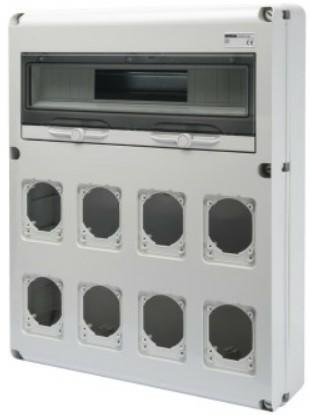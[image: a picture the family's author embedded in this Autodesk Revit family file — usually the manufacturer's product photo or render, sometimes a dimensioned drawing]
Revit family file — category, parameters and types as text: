
# Revit family: Building-QuadriIEC309-GEWISS-68QDIN-QUADRI-PRESE-20MOD_8PRESE
name_source: partatom
category: Apparecchi elettrici
units: mm (PartAtom-declared; Revit-internal decimal feet)

## family parameters
Condiviso = No
Host = Superficie
Mantenere orientamento annotazione = Sì
Punto di calcolo locali = Sì
Quota connettore circolare = Usa diametro
Taglio con vuoti quando caricato = No
Tipo di parte = Normale

## types (1)
- GW68013N - Q-DIN 20M 8FLANGE PR.16/32A IP65
    Catalogo = BUILDING
    Catalogo Serie = 68 QDIN
    Classe isolamento = II
    Codice EAN = 8011564744905
    Codice Electrocod = 2242
    Colore = Grigio RAL 7035
    Conformità normativa = EN 60208 - EN 60670-1 - IEC 60670-24
    Descrizione = Q-DIN 20M 8FLANGE PR.16/32A IP65
    Glow Wire Test = 650°C
    Grado di protezione = IP65
    IDF = d9efa6a9-06b7-4b9e-bedb-9bde757b1bb5
    IDT = 3b58a0f8-96cf-43f3-8e98-bcad634a41cb
    Immagine tipo = GW68013N.jpg
    L_Moduli = 380 mm  [stored 1.24672 ft]
    Modello = GW68013N
    N. coperchi ciechi in dotazione = 2 IEC 16/32 A
    N. mod. EN 50022 = 20
    N. prese alloggiabili = 8 IEC 309 16/32 A IP44/67
    N_Moduli = 20 mm  [stored 0.0656168 ft]
    POMELLO = bianco
    PRESA = rosso
    Potenza dissipabile A (W) = 30
    Potenza dissipabile B (W) = 92
    Produttore = GEWISS S.p.A.
    Prospetto di default = 1219 mm
    Resistenza agli urti = IK08
    SEO = Quadretto
    STRUTTURA = RAL - 7035
    STRUTTURA ALTA = Poche
    Scheda Tecnica = https://www.gewiss.com
    Spostamento_S = 1000 mm  [stored 3.28084 ft]
    Temperatura di utilizzo = -25 +40 °C
    Termopressione con biglia = 70 °C
    Tipo versione = Vuoto
    Tipologia di installazione = Da parete
    URL = https://www.gewiss.com
    VETRO = Vetro
    Versione file RFA = 21.5

note: [stored X ft] marks values corroborated as IEEE doubles in the binary element streams (Revit-internal decimal feet)

## geometry (parser evidence)
native form markers: Sweep x3
no freeform markers — native parametric forms only
